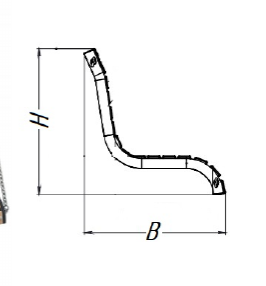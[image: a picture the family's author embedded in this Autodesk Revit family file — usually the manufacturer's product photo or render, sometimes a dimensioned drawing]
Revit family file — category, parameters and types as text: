
# Revit family: Качели подвесные «Сочи» Арт 15277
name_source: partatom
category: Антураж
revit_build: Autodesk Revit 2018 (Build: 20180423_1000(x64)
units: mm (PartAtom-declared; Revit-internal decimal feet)

## family parameters
Всегда вертикально = Да
Источник визуального образа = Геометрия семейства
На основе рабочей плоскости = Нет
Общий = Нет
При загрузке вырезать с полостями = Нет
Точка расчета площади = Нет

## types (2) — shared parameters
URL = https://hobbyka.ru
Артикул товара = Арт. 15277
Высота = 665 мм
Группа модели = Садовая и дачная мебель
Изготовитель = ООО «Хоббика
Изображение типоразмера = Качели подвесные «Сочи» Арт 15277.jpg
Материал изделия = Сталь, дерево
Цвет каркаса = Сталь
Цвет сидения = Дерево
Ширина = 650 мм

## per-type parameters (varying)
| type | Версия 1,5 м | Версия 1,8 м | Длина |
| Качели подвесные «Сочи». Версия 1,5 м | Да | Нет | 1500 мм |
| Качели подвесные «Сочи». Версия 1,8 м | Нет | Да | 1800 мм |

note: column(s) folded — value = type name in every type: Описание
